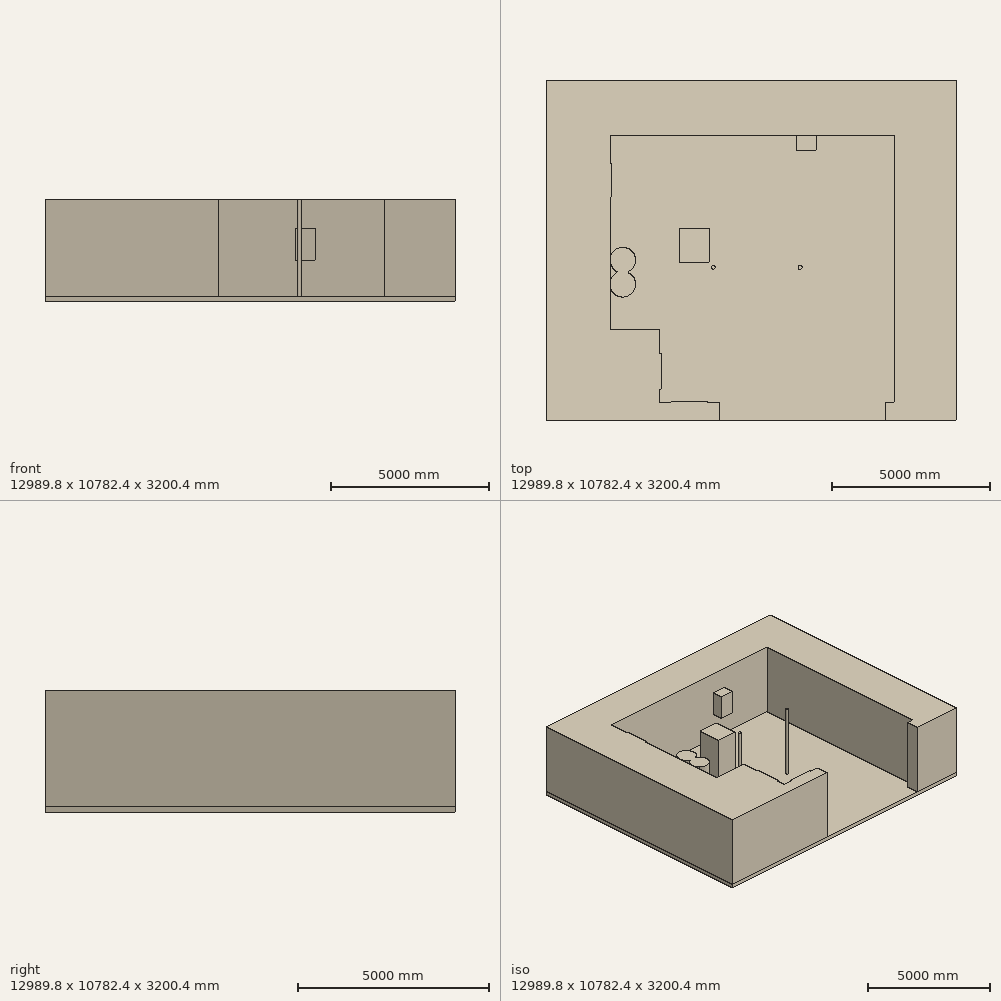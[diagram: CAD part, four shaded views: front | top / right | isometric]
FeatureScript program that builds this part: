
annotation { "Feature Type Name" : "Feature", "Feature Type Description" : "" }
export const myFeature = defineFeature(function(context is Context, id is Id, definition is map)
    precondition{}
    {
        {
            var Q0;
            Q0=qCreatedBy(makeId("Top.planeOp"),FACE);
            var sketch = newSketch(context, id + "F0", { "sketchPlane" : qUnion([Q0])});
            skLineSegment(sketch, "E0", {"start": v(-4497.59, 3670.5) * mm, "end": v(-4497.59, 2806.9) * mm});
            skLineSegment(sketch, "E1", {"start": v(-4497.59, -2450.9) * mm, "end": v(-2922.79, -2450.9) * mm});
            skLineSegment(sketch, "E2", {"start": v(-2922.79, -2450.9) * mm, "end": v(-2922.79, -3212.9) * mm});
            skLineSegment(sketch, "E3", {"start": v(-2922.79, -4787.7) * mm, "end": v(-2541.79, -4787.7) * mm});
            skLineSegment(sketch, "E4", {"start": v(4519.41, -4787.7) * mm, "end": v(4519.41, 3670.5) * mm});
            skLineSegment(sketch, "E5", {"start": v(4519.41, 3670.5) * mm, "end": v(2030.21, 3670.5) * mm});
            skLineSegment(sketch, "E6.bottom", {"start": v(-2414.79, 876.5) * mm, "end": v(-1068.59, 876.5) * mm, "construction": true});
            skLineSegment(sketch, "E6.top", {"start": v(-2414.79, -647.5) * mm, "end": v(-1068.59, -647.5) * mm, "construction": true});
            skLineSegment(sketch, "E6.left", {"start": v(-2414.79, 876.5) * mm, "end": v(-2414.79, -647.5) * mm, "construction": true});
            skLineSegment(sketch, "E6.right", {"start": v(-1068.59, 876.5) * mm, "end": v(-1068.59, -647.5) * mm, "construction": true});
            skCircle(sketch, "E7", {"center": v(-1220.99, -495.1) * mm, "radius": 63.5 * mm});
            skCircle(sketch, "E8", {"center": v(1522.21, -495.1) * mm, "radius": 63.5 * mm});
            skLineSegment(sketch, "E9.bottom", {"start": v(-1017.79, -4787.7) * mm, "end": v(-1398.79, -4787.7) * mm});
            skLineSegment(sketch, "E9.top", {"start": v(-1017.79, -5348.72) * mm, "end": v(-6512.1, -5348.72) * mm});
            skLineSegment(sketch, "E9.left", {"start": v(-1017.79, -4787.7) * mm, "end": v(-1017.79, -5348.72) * mm});
            skLineSegment(sketch, "E9.right", {"start": v(-6512.1, -4787.7) * mm, "end": v(-6512.1, -5348.72) * mm});
            skLineSegment(sketch, "E10", {"start": v(-6512.1, -4787.7) * mm, "end": v(-6512.1, 5433.69) * mm});
            skLineSegment(sketch, "E11", {"start": v(-6512.1, 5433.69) * mm, "end": v(6477.68, 5433.69) * mm});
            skLineSegment(sketch, "E12", {"start": v(6477.68, 5433.69) * mm, "end": v(6477.68, -5348.72) * mm});
            skLineSegment(sketch, "E13", {"start": v(6477.68, -5348.72) * mm, "end": v(4214.61, -5348.72) * mm});
            skLineSegment(sketch, "E14", {"start": v(4214.61, -5348.72) * mm, "end": v(4214.61, -4787.7) * mm});
            skLineSegment(sketch, "E15.trimOffspring", {"start": v(4214.61, -4787.7) * mm, "end": v(4519.41, -4787.7) * mm});
            skLineSegment(sketch, "E16.trimOffspring", {"start": v(1395.21, 3670.5) * mm, "end": v(-4497.59, 3670.5) * mm});
            skLineSegment(sketch, "E17.trimOffspring", {"start": v(-4497.59, -1434.9) * mm, "end": v(-4497.59, -2450.9) * mm});
            skLineSegment(sketch, "E18.bottom", {"start": v(-4497.59, 2806.9) * mm, "end": v(-4446.79, 2806.9) * mm});
            skLineSegment(sketch, "E18.top", {"start": v(-4497.59, 1714.7) * mm, "end": v(-4446.79, 1714.7) * mm});
            skLineSegment(sketch, "E18.right", {"start": v(-4446.79, 2806.9) * mm, "end": v(-4446.79, 1714.7) * mm});
            skLineSegment(sketch, "E19.trimOffspring", {"start": v(-4497.59, 1714.7) * mm, "end": v(-4497.59, 139.9) * mm});
            skArc(sketch, "E20", {"start": v(-4232.61, -647.5) * mm, "mid": v(-4091.19, -1434.9) * mm, "end": v(-3949.77, -647.5) * mm});
            skPoint(sketch, "E20.centerSnap0", {"position": v(-4091.19, -1434.9) * mm});
            skArc(sketch, "E21", {"start": v(-3949.77, -647.5) * mm, "mid": v(-4091.19, 139.9) * mm, "end": v(-4232.61, -647.5) * mm});
            skLineSegment(sketch, "E22", {"start": v(-4497.59, 139.9) * mm, "end": v(-4497.59, -266.5) * mm});
            skLineSegment(sketch, "E23", {"start": v(-4497.59, -1028.5) * mm, "end": v(-4497.59, -1434.9) * mm});
            skPoint(sketch, "E24.orphan", {"position": v(-3684.79, -1434.9) * mm});
            skLineSegment(sketch, "E25", {"start": v(-4497.59, -266.5) * mm, "end": v(-4497.59, -1028.5) * mm});
            skLineSegment(sketch, "E26.bottom", {"start": v(-2287.55, 738.92) * mm, "end": v(-1334.62, 738.92) * mm});
            skLineSegment(sketch, "E26.top", {"start": v(-2287.55, -325.39) * mm, "end": v(-1334.62, -325.39) * mm});
            skLineSegment(sketch, "E26.left", {"start": v(-2287.55, 738.92) * mm, "end": v(-2287.55, -325.39) * mm});
            skLineSegment(sketch, "E26.right", {"start": v(-1334.62, 738.92) * mm, "end": v(-1334.62, -325.39) * mm});
            skLineSegment(sketch, "E27.bottom", {"start": v(-2922.79, -3212.9) * mm, "end": v(-2871.99, -3212.9) * mm});
            skLineSegment(sketch, "E27.top", {"start": v(-2922.79, -4355.9) * mm, "end": v(-2871.99, -4355.9) * mm});
            skLineSegment(sketch, "E27.right", {"start": v(-2871.99, -3212.9) * mm, "end": v(-2871.99, -4355.9) * mm});
            skLineSegment(sketch, "E28.trimOffspring", {"start": v(-2922.79, -4355.9) * mm, "end": v(-2922.79, -4787.7) * mm});
            skLineSegment(sketch, "E29.top", {"start": v(-2541.79, -4736.9) * mm, "end": v(-1398.79, -4736.9) * mm});
            skLineSegment(sketch, "E29.left", {"start": v(-2541.79, -4787.7) * mm, "end": v(-2541.79, -4736.9) * mm});
            skLineSegment(sketch, "E29.right", {"start": v(-1398.79, -4787.7) * mm, "end": v(-1398.79, -4736.9) * mm});
            skLineSegment(sketch, "E30.trimOffspring", {"start": v(-1398.79, -4787.7) * mm, "end": v(-1017.79, -4787.7) * mm});
            skLineSegment(sketch, "E31.trimOffspring", {"start": v(-2541.79, -4787.7) * mm, "end": v(-2922.79, -4787.7) * mm});
            skLineSegment(sketch, "E32", {"start": v(1395.21, 3670.5) * mm, "end": v(2030.21, 3670.5) * mm});
            skSolve(sketch);
        }
        {
            var Q0;
            Q0=makeQuery(id+"F0.imprint","IMPRINT",FACE,{"disambiguationData":[TD([[makeQuery(id+"F0.imprint","IMPRINT",EDGE,{"derivedFrom":sQuery(id+"F0.wireOp",EDGE,"E0")}),-1.0]])]});
            var Q1;
            Q1=makeQuery(id+"F0.imprint","IMPRINT",FACE,{"disambiguationData":[TD([[makeQuery(id+"F0.imprint","IMPRINT",EDGE,{"derivedFrom":sQuery(id+"F0.wireOp",EDGE,"E6.bottom")}),-1.0]])]});
            var Q2;
            Q2=makeQuery(id+"F0.imprint","IMPRINT",FACE,{"disambiguationData":[TD([[makeQuery(id+"F0.imprint","IMPRINT",EDGE,{"derivedFrom":sQuery(id+"F0.wireOp",EDGE,"E8")}),1.0]])]});
            var Q3;
            Q3=makeQuery(id+"F0.imprint","IMPRINT",FACE,{"disambiguationData":[TD([[makeQuery(id+"F0.imprint","IMPRINT",EDGE,{"derivedFrom":sQuery(id+"F0.wireOp",EDGE,"E26.bottom")}),-1.0]])]});
            var Q4;
            {var subQ0=sQuery(id+"F0.wireOp",EDGE,"E21");var subQ1=sQuery(id+"F0.wireOp",EDGE,"E20");var subQ2=makeQuery(id+"F0.imprint","INTERSECT",VERTEX,{"disambiguationData":[OD(0.0)],"derivedFrom":[subQ1,subQ0]});Q4=makeQuery(id+"F0.imprint","IMPRINT",FACE,{"disambiguationData":[TD([[makeQuery(id+"F0.imprint","IMPRINT",EDGE,{"disambiguationData":[TD([[subQ2,-1.0]])],"derivedFrom":subQ1}),1.0]])]});}
            var Q5;
            Q5=makeQuery(id+"F0.imprint","IMPRINT",FACE,{"disambiguationData":[TD([[makeQuery(id+"F0.imprint","IMPRINT",EDGE,{"derivedFrom":sQuery(id+"F0.wireOp",EDGE,"E7")}),1.0]])]});
            extrude(context, id + "F1", {"entities" : qUnion([Q0, Q1, Q2, Q3, Q4, Q5]), "depth" : 3048 * mm, "offsetDistance" : 25.4 * mm});
        }
        {
            var Q0;
            Q0=makeQuery(id+"F1.opExtrude","CAP_FACE",FACE,{"disambiguationData":[OSD([sQuery(id+"F0.wireOp",EDGE,"E0"),sQuery(id+"F0.wireOp",EDGE,"E1"),sQuery(id+"F0.wireOp",EDGE,"E2"),sQuery(id+"F0.wireOp",EDGE,"E4"),sQuery(id+"F0.wireOp",EDGE,"E5"),sQuery(id+"F0.wireOp",EDGE,"MzTzpKCl-0bQI-QTcn-QW0N-TxIAlEzpdIn1.top"),sQuery(id+"F0.wireOp",EDGE,"MzTzpKCl-0bQI-QTcn-QW0N-TxIAlEzpdIn1.left"),sQuery(id+"F0.wireOp",EDGE,"MzTzpKCl-0bQI-QTcn-QW0N-TxIAlEzpdIn1.right"),sQuery(id+"F0.wireOp",EDGE,"zSFwF5x7-qe31-woca-XuIq-f5GbwR88uNuc.bottom"),sQuery(id+"F0.wireOp",EDGE,"zSFwF5x7-qe31-woca-XuIq-f5GbwR88uNuc.top"),sQuery(id+"F0.wireOp",EDGE,"zSFwF5x7-qe31-woca-XuIq-f5GbwR88uNuc.right"),sQuery(id+"F0.wireOp",EDGE,"E9.bottom"),sQuery(id+"F0.wireOp",EDGE,"E9.top"),sQuery(id+"F0.wireOp",EDGE,"E9.left"),sQuery(id+"F0.wireOp",EDGE,"E9.right"),sQuery(id+"F0.wireOp",EDGE,"E10"),sQuery(id+"F0.wireOp",EDGE,"E11"),sQuery(id+"F0.wireOp",EDGE,"E12"),sQuery(id+"F0.wireOp",EDGE,"E13"),sQuery(id+"F0.wireOp",EDGE,"E14"),sQuery(id+"F0.wireOp",EDGE,"E15.trimOffspring"),sQuery(id+"F0.wireOp",EDGE,"E16.trimOffspring"),sQuery(id+"F0.wireOp",EDGE,"E17.trimOffspring"),sQuery(id+"F0.wireOp",EDGE,"E18.bottom"),sQuery(id+"F0.wireOp",EDGE,"E18.top"),sQuery(id+"F0.wireOp",EDGE,"E18.right"),sQuery(id+"F0.wireOp",EDGE,"E19.trimOffspring")])],"isStart":true});
            var sketch = newSketch(context, id + "F2", { "sketchPlane" : qUnion([Q0])});
            skLineSegment(sketch, "E33.bottom", {"start": v(-6512.1, 5348.72) * mm, "end": v(6477.68, 5348.72) * mm});
            skLineSegment(sketch, "E33.top", {"start": v(-6512.1, -5433.69) * mm, "end": v(6477.68, -5433.69) * mm});
            skLineSegment(sketch, "E33.left", {"start": v(-6512.1, 5348.72) * mm, "end": v(-6512.1, -5433.69) * mm});
            skLineSegment(sketch, "E33.right", {"start": v(6477.68, 5348.72) * mm, "end": v(6477.68, -5433.69) * mm});
            skSolve(sketch);
        }
        {
            var Q0;
            Q0 = qSketchRegion(id + "F2", true);
            extrude(context, id + "F3", {"entities" : qUnion([Q0]), "depth" : 152.4 * mm, "offsetDistance" : 25.4 * mm});
        }
        {
            var Q0;
            Q0=makeQuery(id+"F1.opExtrude","SWEPT_FACE",FACE,{"disambiguationData":[OSD([sQuery(id+"F0.wireOp",EDGE,"E5"),sQuery(id+"F0.wireOp",EDGE,"E16.trimOffspring"),sQuery(id+"F0.wireOp",EDGE,"E32")])]});
            var sketch = newSketch(context, id + "F4", { "sketchPlane" : qUnion([Q0])});
            skLineSegment(sketch, "E34.bottom", {"start": v(1395.21, 2159) * mm, "end": v(2030.21, 2159) * mm});
            skLineSegment(sketch, "E34.top", {"start": v(1395.21, 1143) * mm, "end": v(2030.21, 1143) * mm});
            skLineSegment(sketch, "E34.left", {"start": v(1395.21, 2159) * mm, "end": v(1395.21, 1143) * mm});
            skLineSegment(sketch, "E34.right", {"start": v(2030.21, 2159) * mm, "end": v(2030.21, 1143) * mm});
            skSolve(sketch);
        }
        {
            var Q0;
            Q0=makeQuery(id+"F4.imprint","IMPRINT",FACE,{"disambiguationData":[TD([[makeQuery(id+"F4.imprint","IMPRINT",EDGE,{"derivedFrom":sQuery(id+"F4.wireOp",EDGE,"E34.bottom")}),-1.0]])]});
            extrude(context, id + "F5", {"entities" : qUnion([Q0]), "operationType" : NewBodyOperationType.ADD, "depth" : 457.2 * mm, "offsetDistance" : 25.4 * mm});
        }
    });
